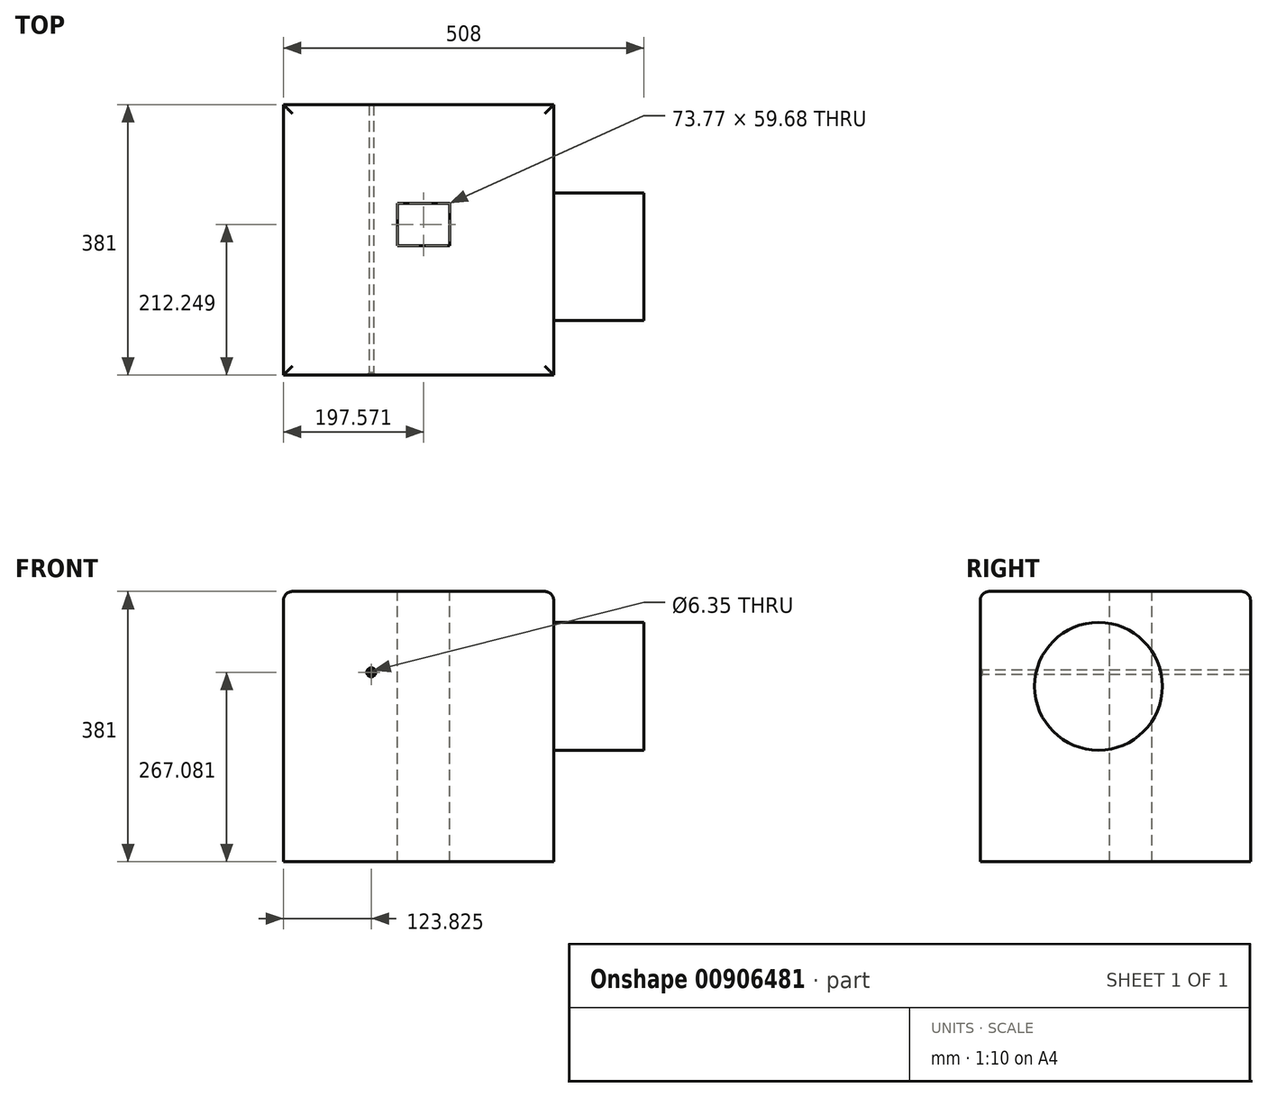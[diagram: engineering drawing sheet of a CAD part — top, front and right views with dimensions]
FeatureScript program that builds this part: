
annotation { "Feature Type Name" : "Feature", "Feature Type Description" : "" }
export const myFeature = defineFeature(function(context is Context, id is Id, definition is map)
    precondition{}
    {
        {
            var Q0;
            Q0=qCreatedBy(makeId("Front.planeOp"),FACE);
            var sketch = newSketch(context, id + "F0", { "sketchPlane" : qUnion([Q0])});
            skLineSegment(sketch, "E0.bottom", {"start": v(0, 0) * mm, "end": v(381, 0) * mm});
            skLineSegment(sketch, "E0.top", {"start": v(0, 381) * mm, "end": v(381, 381) * mm});
            skLineSegment(sketch, "E0.left", {"start": v(0, 0) * mm, "end": v(0, 381) * mm});
            skLineSegment(sketch, "E0.right", {"start": v(381, 0) * mm, "end": v(381, 381) * mm});
            skSolve(sketch);
        }
        {
            var Q0;
            Q0=qSketchRegion(id+"F0",true);
            extrude(context, id + "F1", {"entities" : qUnion([Q0]), "depth" : 381 * mm, "offsetDistance" : 25.4 * mm});
        }
        {
            var Q0;
            Q0=makeQuery(id+"F1.opExtrude","CAP_FACE",FACE,{"disambiguationData":[OSD([sQuery(id+"F0.wireOp",EDGE,"E0.bottom"),sQuery(id+"F0.wireOp",EDGE,"E0.top"),sQuery(id+"F0.wireOp",EDGE,"E0.left"),sQuery(id+"F0.wireOp",EDGE,"E0.right")])],"isStart":false});
            var sketch = newSketch(context, id + "F2", { "sketchPlane" : qUnion([Q0])});
            skPoint(sketch, "E1", {"position": v(123.83, 267.08) * mm});
            skSolve(sketch);
        }
        {
            var Q0;
            Q0=sQuery(id+"F2.wireOp",VERTEX,"E1");
            var Q1;
            Q1=makeQuery(id+"F1.opExtrude","SWEPT_BODY",BODY,{"disambiguationData":[OSD([sQuery(id+"F0.wireOp",EDGE,"E0.bottom"),sQuery(id+"F0.wireOp",EDGE,"E0.top"),sQuery(id+"F0.wireOp",EDGE,"E0.left"),sQuery(id+"F0.wireOp",EDGE,"E0.right")])]});
            hole(context, id + "F3", {"style" : HoleStyle.C_SINK, "endStyle" : HoleEndStyle.THROUGH, "holeDiameter" : 6.35 * mm, "cSinkDiameter" : 12.7 * mm, "cSinkAngle" : 90 * degree, "majorDiameter" : 6.35 * mm, "isTappedThrough" : true, "tappedDepth" : 12.7 * mm, "tapClearance" : 3, "locations" : qUnion([Q0]), "scope" : qUnion([Q1])});
        }
        {
            var Q0;
            Q0=makeQuery(id+"F1.opExtrude","SWEPT_FACE",FACE,{"disambiguationData":[OSD([sQuery(id+"F0.wireOp",EDGE,"E0.top")])]});
            fillet(context, id + "F4", {"entities" : qUnion([Q0]), "radius" : 12.7 * mm, "tangentPropagation" : true, "allowEdgeOverflow" : false});
        }
        {
            var Q0;
            Q0=makeQuery(id+"F1.opExtrude","SWEPT_FACE",FACE,{"disambiguationData":[OSD([sQuery(id+"F0.wireOp",EDGE,"E0.right")])]});
            var sketch = newSketch(context, id + "F5", { "sketchPlane" : qUnion([Q0])});
            skCircle(sketch, "E2", {"center": v(-214.3, 247.3) * mm, "radius": 90.07 * mm});
            skSolve(sketch);
        }
        {
            var Q0;
            Q0=qSketchRegion(id+"F5",true);
            extrude(context, id + "F6", {"entities" : qUnion([Q0]), "operationType" : NewBodyOperationType.ADD, "depth" : 127 * mm, "offsetDistance" : 25.4 * mm});
        }
        {
            var Q0;
            Q0=makeQuery(id+"F1.opExtrude","SWEPT_FACE",FACE,{"disambiguationData":[OSD([sQuery(id+"F0.wireOp",EDGE,"E0.top")])]});
            var sketch = newSketch(context, id + "F7", { "sketchPlane" : qUnion([Q0])});
            skLineSegment(sketch, "E3.bottom", {"start": v(160.68, -198.6) * mm, "end": v(234.46, -198.6) * mm});
            skLineSegment(sketch, "E3.top", {"start": v(160.68, -138.91) * mm, "end": v(234.46, -138.91) * mm});
            skLineSegment(sketch, "E3.left", {"start": v(160.68, -198.6) * mm, "end": v(160.68, -138.91) * mm});
            skLineSegment(sketch, "E3.right", {"start": v(234.46, -198.6) * mm, "end": v(234.46, -138.91) * mm});
            skSolve(sketch);
        }
        {
            var Q0;
            Q0 = qSketchRegion(id + "F7", true);
            extrude(context, id + "F8", {"entities" : qUnion([Q0]), "operationType" : NewBodyOperationType.REMOVE, "oppositeDirection" : true, "depth" : 508 * mm, "offsetDistance" : 25.4 * mm});
        }
    });
